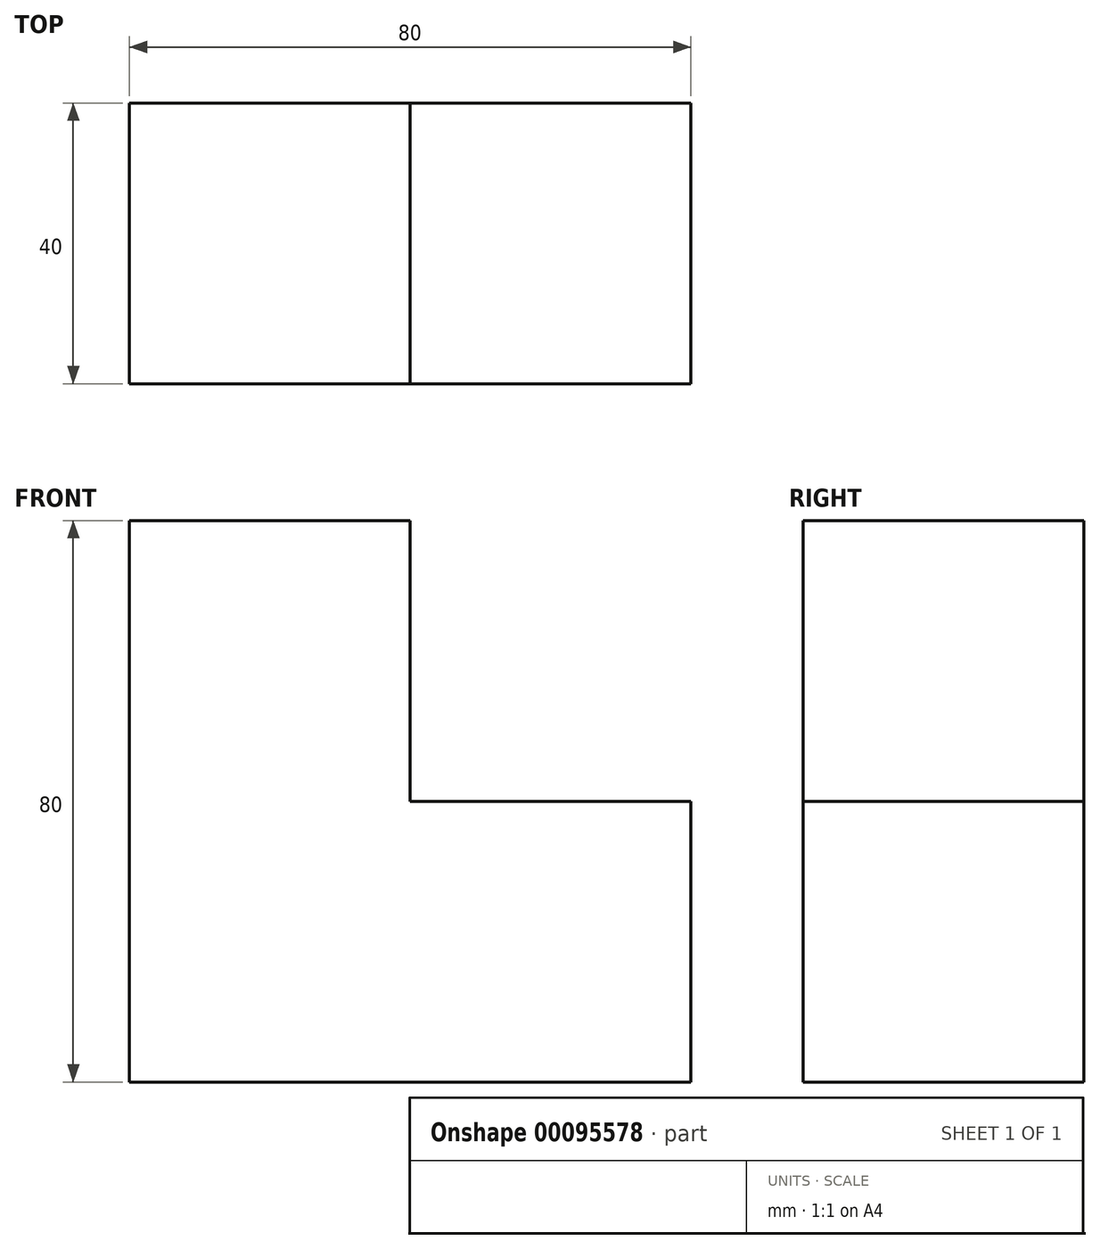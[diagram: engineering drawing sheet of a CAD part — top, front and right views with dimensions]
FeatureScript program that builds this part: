
annotation { "Feature Type Name" : "Feature", "Feature Type Description" : "" }
export const myFeature = defineFeature(function(context is Context, id is Id, definition is map)
    precondition{}
    {
        {
            var Q0;
            Q0=qCreatedBy(makeId("Front.planeOp"),FACE);
            var sketch = newSketch(context, id + "F0", { "sketchPlane" : qUnion([Q0])});
            skLineSegment(sketch, "E0", {"start": v(-40, 40) * mm, "end": v(-40, -40) * mm});
            skLineSegment(sketch, "E1", {"start": v(-40, -40) * mm, "end": v(40, -40) * mm});
            skLineSegment(sketch, "E2", {"start": v(40, -40) * mm, "end": v(40, 0) * mm});
            skLineSegment(sketch, "E3", {"start": v(40, 0) * mm, "end": v(0, 0) * mm});
            skLineSegment(sketch, "E4", {"start": v(0, 0) * mm, "end": v(0, 40) * mm});
            skLineSegment(sketch, "E5", {"start": v(0, 40) * mm, "end": v(-40, 40) * mm});
            skSolve(sketch);
        }
        {
            var Q0;
            Q0=makeQuery(id+"F0.imprint","IMPRINT",FACE,{"disambiguationData":[TD([[makeQuery(id+"F0.imprint","IMPRINT",EDGE,{"derivedFrom":sQuery(id+"F0.wireOp",EDGE,"E0")}),1.0]])]});
            extrude(context, id + "F1", {"entities" : qUnion([Q0]), "depth" : 40 * mm});
        }
    });
